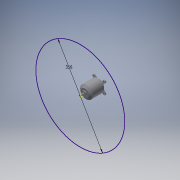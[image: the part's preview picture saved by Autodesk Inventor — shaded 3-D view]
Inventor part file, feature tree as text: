
AUTODESK INVENTOR PART (.ipt)
format: ipt  version: 2018 (Build 220112000, 112)  size: 184,832 bytes
history: native  units: in
note: dims shown in document units (in); Inventor stores cm internally (conversion verified against a paired STEP export)
features: sketch x6, extrude x2, other x2, chamfer x1, plane x1, revolve x1
ambient origin geometry x8: Origin, YZ Plane, XZ Plane, XY Plane, X Axis, Y Axis, Z Axis, Center Point
bodies: Solid1 (feature_tree)
feature tree (13):
  extrude  "Extrusion1"  TaperAngle=135.0deg  [1 undecoded]
  extrude  "Extrusion2"  TaperAngle=45.0deg  [1 undecoded]
  chamfer  "Chamfer1"  Distance=0.1575in
  sketch  "Sketch3"  dims[d4=0.0984in]
  other  "Work Axis1"
  other  "Work Point1"
  sketch  "Sketch4"  dims[d5=0.0984in]
  plane  "Work Plane1"
  revolve  "Revolution1"  [1 undecoded]
  sketch  "Sketch6"  dims[d7=0.1969in d8=0.1575in d9=0.0in d10=0.9846in d11=1.9685in d12=0.0in d13=0.1575in d14=0.0787in d15=45.0deg d16=0.9843in d17=0.1181in d18=0.5906in d19=0.1969in d20=0.1476in d21=0.315in d22=90.0deg d23=14.0157in]
  sketch  "Sketch1"  dims[d0=1.1535in d1=135.0deg]
  sketch  "Sketch2"  dims[d2=1.1535in d3=45.0deg]
  sketch  "Sketch5"  dims[d6=0.1969in]
note: 3 required parameter values undecoded (feature->parameter linkage not recoverable at this tier; creation-order binding heuristic only, values carry confidence <= 0.55)